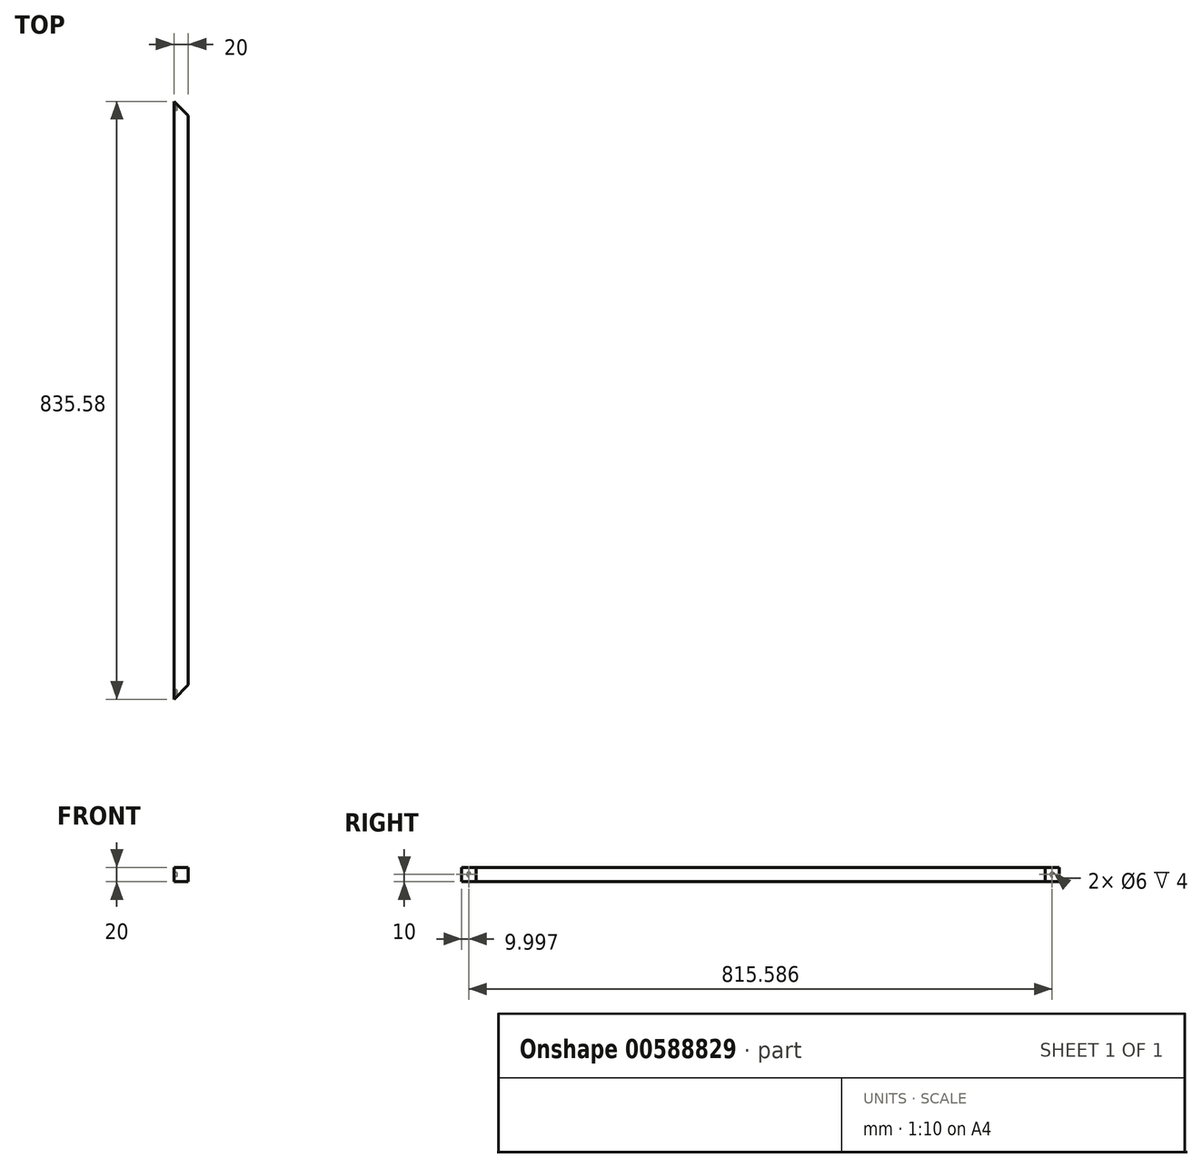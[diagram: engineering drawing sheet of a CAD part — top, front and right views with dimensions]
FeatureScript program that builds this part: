
annotation { "Feature Type Name" : "Feature", "Feature Type Description" : "" }
export const myFeature = defineFeature(function(context is Context, id is Id, definition is map)
    precondition{}
    {
        {
            var Q0;
            Q0=qCreatedBy(makeId("Front.planeOp"),FACE);
            var sketch = newSketch(context, id + "F0", { "sketchPlane" : qUnion([Q0])});
            skLineSegment(sketch, "E0.bottom", {"start": v(0, 0) * mm, "end": v(20, 0) * mm});
            skLineSegment(sketch, "E0.top", {"start": v(0, 20) * mm, "end": v(20, 20) * mm});
            skLineSegment(sketch, "E0.left", {"start": v(0, 0) * mm, "end": v(0, 20) * mm});
            skLineSegment(sketch, "E0.right", {"start": v(20, 0) * mm, "end": v(20, 20) * mm});
            skSolve(sketch);
        }
        {
            var Q0;
            Q0=makeQuery(id+"F0.imprint","IMPRINT",FACE,{"disambiguationData":[TD([[makeQuery(id+"F0.imprint","IMPRINT",EDGE,{"derivedFrom":sQuery(id+"F0.wireOp",EDGE,"E0.bottom")}),1.0]])]});
            extrude(context, id + "F1", {"entities" : qUnion([Q0]), "depth" : 835.6 * mm, "offsetDistance" : 25 * mm, "symmetric" : true});
        }
        {
            var Q0;
            Q0=makeQuery(id+"F1.opExtrude","CAP_EDGE",EDGE,{"disambiguationData":[OSD([sQuery(id+"F0.wireOp",EDGE,"E0.right")])],"isStart":false});
            chamfer(context, id + "F2", {"entities" : qUnion([Q0]), "chamferType" : ChamferType.OFFSET_ANGLE, "width" : 20 * mm, "oppositeDirection" : false, "angle" : 45 * degree, "tangentPropagation" : true});
        }
        {
            var Q0;
            Q0=makeQuery(id+"F1.opExtrude","CAP_EDGE",EDGE,{"disambiguationData":[OSD([sQuery(id+"F0.wireOp",EDGE,"E0.right")])],"isStart":true});
            chamfer(context, id + "F3", {"entities" : qUnion([Q0]), "width" : 20 * mm, "tangentPropagation" : true});
        }
        {
            var Q0;
            Q0=makeQuery(id+"F1.opExtrude","SWEPT_FACE",FACE,{"disambiguationData":[OSD([sQuery(id+"F0.wireOp",EDGE,"E0.left")])]});
            var sketch = newSketch(context, id + "F4", { "sketchPlane" : qUnion([Q0])});
            skCircle(sketch, "E1", {"center": v(-407.8, 10) * mm, "radius": 3 * mm});
            skSolve(sketch);
        }
        {
            var Q0;
            Q0=makeQuery(id+"F4.imprint","IMPRINT",FACE,{"disambiguationData":[TD([[makeQuery(id+"F4.imprint","IMPRINT",EDGE,{"derivedFrom":sQuery(id+"F4.wireOp",EDGE,"E1")}),1.0]])]});
            extrude(context, id + "F5", {"entities" : qUnion([Q0]), "operationType" : NewBodyOperationType.REMOVE, "oppositeDirection" : true, "depth" : 4 * mm, "offsetDistance" : 25 * mm});
        }
        {
            var Q0;
            Q0=makeQuery(id+"F1.opExtrude","SWEPT_FACE",FACE,{"disambiguationData":[OSD([sQuery(id+"F0.wireOp",EDGE,"E0.left")])]});
            var sketch = newSketch(context, id + "F6", { "sketchPlane" : qUnion([Q0])});
            skCircle(sketch, "E2", {"center": v(407.8, 10) * mm, "radius": 3 * mm});
            skSolve(sketch);
        }
        {
            var Q0;
            Q0=makeQuery(id+"F6.imprint","IMPRINT",FACE,{"disambiguationData":[TD([[makeQuery(id+"F6.imprint","IMPRINT",EDGE,{"derivedFrom":sQuery(id+"F6.wireOp",EDGE,"E2")}),1.0]])]});
            extrude(context, id + "F7", {"entities" : qUnion([Q0]), "operationType" : NewBodyOperationType.REMOVE, "oppositeDirection" : true, "depth" : 4 * mm, "offsetDistance" : 25 * mm});
        }
    });
